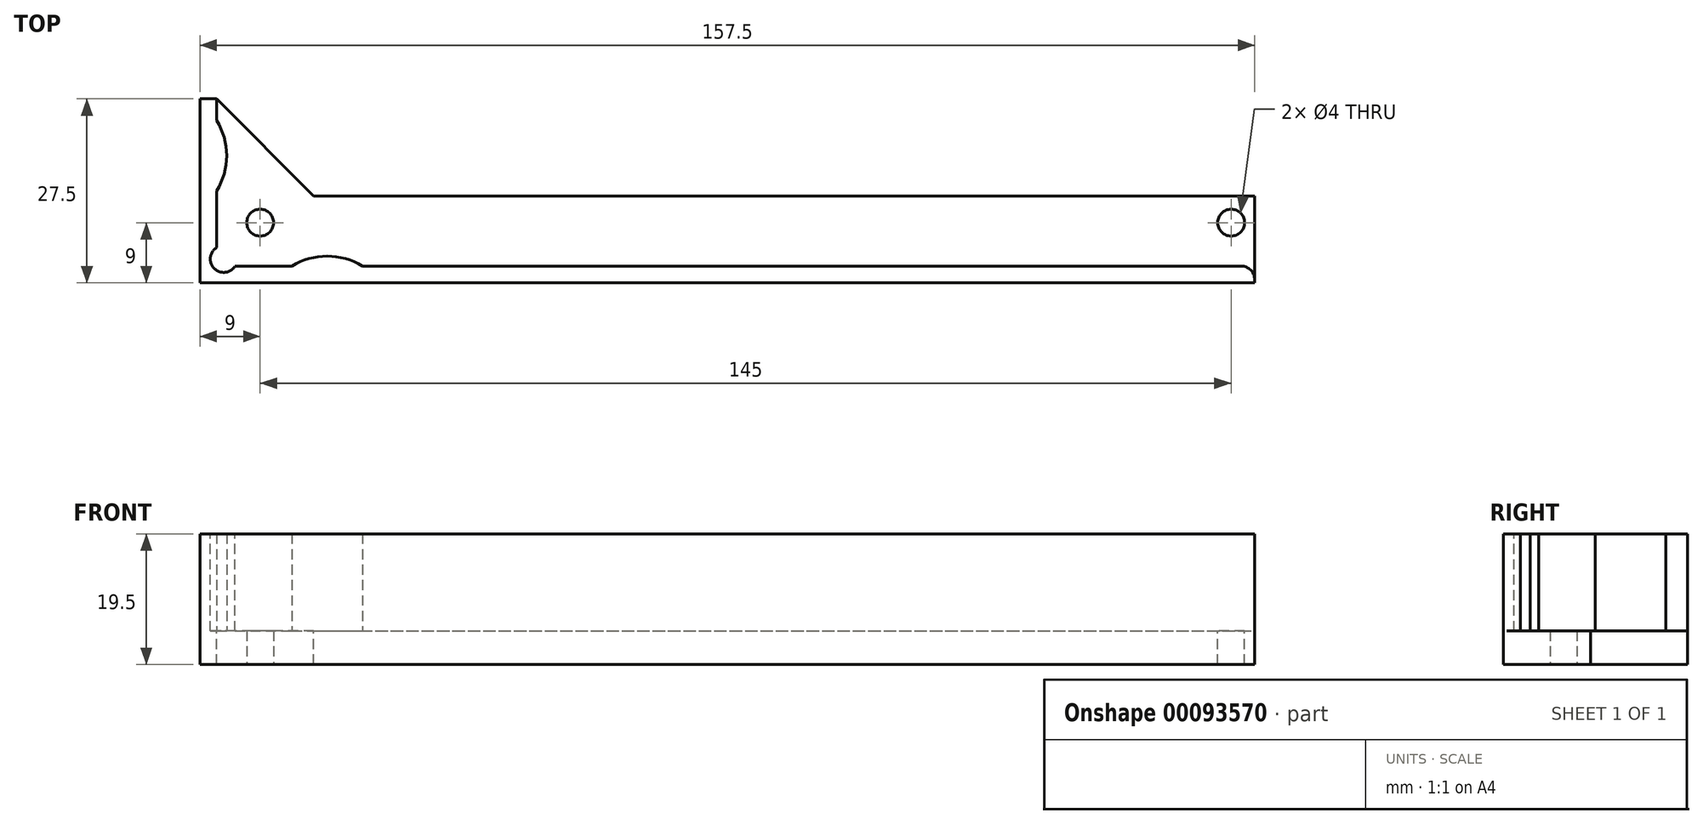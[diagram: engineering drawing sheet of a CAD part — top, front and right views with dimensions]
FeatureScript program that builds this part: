
annotation { "Feature Type Name" : "Feature", "Feature Type Description" : "" }
export const myFeature = defineFeature(function(context is Context, id is Id, definition is map)
    precondition{}
    {
        {
            var Q0;
            Q0=qCreatedBy(makeId("Top.planeOp"),FACE);
            var sketch = newSketch(context, id + "F0", { "sketchPlane" : qUnion([Q0])});
            skCircle(sketch, "E0", {"center": v(0, 0) * mm, "radius": 2 * mm});
            skLineSegment(sketch, "E1", {"start": v(-9, -21) * mm, "end": v(-9, 9) * mm});
            skLineSegment(sketch, "E2", {"start": v(-9, 9) * mm, "end": v(21, 9) * mm});
            skLineSegment(sketch, "E3", {"start": v(21, 9) * mm, "end": v(-9, -21) * mm});
            skSolve(sketch);
        }
        {
            var Q0;
            Q0=qSketchRegion(id+"F0",true);
            extrude(context, id + "F1", {"entities" : qUnion([Q0]), "depth" : 5 * mm});
        }
        {
            var Q0;
            Q0=makeQuery(id+"F1.opExtrude","CAP_FACE",FACE,{"disambiguationData":[OSD([sQuery(id+"F0.wireOp",EDGE,"E0"),sQuery(id+"F0.wireOp",EDGE,"E1"),sQuery(id+"F0.wireOp",EDGE,"E2"),sQuery(id+"F0.wireOp",EDGE,"E3")])],"isStart":false});
            var sketch = newSketch(context, id + "F2", { "sketchPlane" : qUnion([Q0])});
            skLineSegment(sketch, "E4.0", {"start": v(-9, -21) * mm, "end": v(-9, 9) * mm});
            skLineSegment(sketch, "E5.0", {"start": v(-9, 9) * mm, "end": v(21, 9) * mm});
            skLineSegment(sketch, "E6", {"start": v(-9, -21) * mm, "end": v(-6.5, -18.5) * mm});
            skLineSegment(sketch, "E7", {"start": v(-6.5, -18.5) * mm, "end": v(-6.5, 6.5) * mm});
            skLineSegment(sketch, "E8", {"start": v(-6.5, 6.5) * mm, "end": v(18.5, 6.5) * mm});
            skLineSegment(sketch, "E9", {"start": v(18.5, 6.5) * mm, "end": v(21, 9) * mm});
            skSolve(sketch);
        }
        {
            var Q0;
            Q0=qSketchRegion(id+"F2",true);
            extrude(context, id + "F3", {"entities" : qUnion([Q0]), "operationType" : NewBodyOperationType.ADD, "depth" : 14.5 * mm});
        }
        {
            var Q0;
            Q0=makeQuery(id+"F3.opExtrude","CAP_FACE",FACE,{"disambiguationData":[OSD([sQuery(id+"F2.wireOp",EDGE,"E4.0"),sQuery(id+"F2.wireOp",EDGE,"E5.0"),sQuery(id+"F2.wireOp",EDGE,"E6"),sQuery(id+"F2.wireOp",EDGE,"E7"),sQuery(id+"F2.wireOp",EDGE,"E8"),sQuery(id+"F2.wireOp",EDGE,"E9")])],"isStart":false});
            var sketch = newSketch(context, id + "F4", { "sketchPlane" : qUnion([Q0])});
            skLineSegment(sketch, "E10", {"start": v(-6.5, 6.5) * mm, "end": v(0, 0) * mm, "construction": true});
            skCircle(sketch, "E11", {"center": v(-5.44, 5.44) * mm, "radius": 2 * mm});
            skSolve(sketch);
        }
        {
            var Q0;
            Q0=qSketchRegion(id+"F4",true);
            var Q1;
            Q1=makeQuery(id+"F1.opExtrude","CAP_FACE",FACE,{"disambiguationData":[OSD([sQuery(id+"F0.wireOp",EDGE,"E0"),sQuery(id+"F0.wireOp",EDGE,"E1"),sQuery(id+"F0.wireOp",EDGE,"E2"),sQuery(id+"F0.wireOp",EDGE,"E3")])],"isStart":false});
            extrude(context, id + "F5", {"entities" : qUnion([Q0]), "operationType" : NewBodyOperationType.REMOVE, "endBound" : BoundingType.UP_TO_SURFACE, "oppositeDirection" : true, "endBoundEntityFace" : qUnion([Q1]), "depth" : 25 * mm});
        }
        {
            var Q0;
            Q0=makeQuery(id+"F3.opExtrude","CAP_FACE",FACE,{"disambiguationData":[OSD([sQuery(id+"F2.wireOp",EDGE,"E4.0"),sQuery(id+"F2.wireOp",EDGE,"E5.0"),sQuery(id+"F2.wireOp",EDGE,"E6"),sQuery(id+"F2.wireOp",EDGE,"E7"),sQuery(id+"F2.wireOp",EDGE,"E8"),sQuery(id+"F2.wireOp",EDGE,"E9")])],"isStart":false});
            var sketch = newSketch(context, id + "F6", { "sketchPlane" : qUnion([Q0])});
            skLineSegment(sketch, "E12", {"start": v(18.5, 6.5) * mm, "end": v(18.5, 18.97) * mm});
            skLineSegment(sketch, "E13", {"start": v(18.5, 18.97) * mm, "end": v(25.37, 18.97) * mm});
            skLineSegment(sketch, "E14", {"start": v(25.37, 18.97) * mm, "end": v(25.37, -18.5) * mm});
            skLineSegment(sketch, "E15", {"start": v(25.37, -18.5) * mm, "end": v(18.5, 6.5) * mm});
            skLineSegment(sketch, "E16", {"start": v(-6.5, -18.5) * mm, "end": v(-15.6, -18.5) * mm});
            skLineSegment(sketch, "E17", {"start": v(-15.6, -18.5) * mm, "end": v(-15.6, -31.56) * mm});
            skLineSegment(sketch, "E18", {"start": v(-15.6, -31.56) * mm, "end": v(-4.83, -31.56) * mm});
            skLineSegment(sketch, "E19", {"start": v(-4.83, -31.56) * mm, "end": v(-6.5, -18.5) * mm});
            skSolve(sketch);
        }
        {
            var Q0;
            Q0=qSketchRegion(id+"F6",true);
            extrude(context, id + "F7", {"entities" : qUnion([Q0]), "operationType" : NewBodyOperationType.REMOVE, "oppositeDirection" : true, "depth" : 25 * mm});
        }
        {
            var Q0;
            Q0=makeQuery(id+"F5.boolean.opBoolean","MERGE",FACE,{"derivedFrom":[makeQuery(id+"F1.opExtrude","CAP_FACE",FACE,{"disambiguationData":[OSD([sQuery(id+"F0.wireOp",EDGE,"E0"),sQuery(id+"F0.wireOp",EDGE,"E1"),sQuery(id+"F0.wireOp",EDGE,"E2"),sQuery(id+"F0.wireOp",EDGE,"E3")])],"isStart":false})],"fromTools":[makeQuery(id+"F5.opExtrude","CAP_FACE",FACE,{"disambiguationData":[OSD([sQuery(id+"F4.wireOp",EDGE,"E11")])],"isStart":false})]});
            var sketch = newSketch(context, id + "F8", { "sketchPlane" : qUnion([Q0])});
            skLineSegment(sketch, "E20", {"start": v(18.5, 6.5) * mm, "end": v(8, -4) * mm});
            skLineSegment(sketch, "E21", {"start": v(8, -4) * mm, "end": v(18.5, -4) * mm});
            skLineSegment(sketch, "E22", {"start": v(18.5, -4) * mm, "end": v(18.5, 6.5) * mm});
            skSolve(sketch);
        }
        {
            var Q0;
            Q0=qSketchRegion(id+"F8",true);
            var Q1;
            Q1=makeQuery(id+"F1.opExtrude","CAP_FACE",FACE,{"disambiguationData":[OSD([sQuery(id+"F0.wireOp",EDGE,"E0"),sQuery(id+"F0.wireOp",EDGE,"E1"),sQuery(id+"F0.wireOp",EDGE,"E2"),sQuery(id+"F0.wireOp",EDGE,"E3")])],"isStart":true});
            extrude(context, id + "F9", {"entities" : qUnion([Q0]), "operationType" : NewBodyOperationType.ADD, "endBound" : BoundingType.UP_TO_SURFACE, "oppositeDirection" : true, "endBoundEntityFace" : qUnion([Q1]), "depth" : 25 * mm});
        }
        {
            var Q0;
            Q0=makeQuery(id+"F9.boolean.opBoolean","MERGE",FACE,{"derivedFrom":[makeQuery(id+"F7.boolean.opBoolean","COPY",FACE,{"derivedFrom":makeQuery(id+"F7.opExtrude","SWEPT_FACE",FACE,{"disambiguationData":[OSD([sQuery(id+"F6.wireOp",EDGE,"E12")])]})}),makeQuery(id+"F9.opExtrude","SWEPT_FACE",FACE,{"disambiguationData":[OSD([sQuery(id+"F8.wireOp",EDGE,"E22")])]})]});
            var sketch = newSketch(context, id + "F10", { "sketchPlane" : qUnion([Q0])});
            skLineSegment(sketch, "E23.0", {"start": v(-4, 0) * mm, "end": v(9, 0) * mm});
            skLineSegment(sketch, "E23.1", {"start": v(9, 19.5) * mm, "end": v(9, 0) * mm});
            skLineSegment(sketch, "E23.2", {"start": v(6.5, 19.5) * mm, "end": v(9, 19.5) * mm});
            skLineSegment(sketch, "E23.3", {"start": v(6.5, 19.5) * mm, "end": v(6.5, 5) * mm});
            skLineSegment(sketch, "E24.0", {"start": v(-4, 5) * mm, "end": v(6.5, 5) * mm});
            skLineSegment(sketch, "E25.0", {"start": v(-4, 0) * mm, "end": v(-4, 5) * mm});
            skSolve(sketch);
        }
        {
            var Q0;
            Q0=qSketchRegion(id+"F10",true);
            extrude(context, id + "F11", {"entities" : qUnion([Q0]), "operationType" : NewBodyOperationType.ADD, "depth" : 154 * mm});
        }
        {
            var Q0;
            Q0=makeQuery(id+"F11.boolean.opBoolean","MERGE",FACE,{"derivedFrom":[makeQuery(id+"F9.boolean.opBoolean","MERGE",FACE,{"derivedFrom":[makeQuery(id+"F5.boolean.opBoolean","MERGE",FACE,{"derivedFrom":[makeQuery(id+"F1.opExtrude","CAP_FACE",FACE,{"disambiguationData":[OSD([sQuery(id+"F0.wireOp",EDGE,"E0"),sQuery(id+"F0.wireOp",EDGE,"E1"),sQuery(id+"F0.wireOp",EDGE,"E2"),sQuery(id+"F0.wireOp",EDGE,"E3")])],"isStart":false})],"fromTools":[makeQuery(id+"F5.opExtrude","CAP_FACE",FACE,{"disambiguationData":[OSD([sQuery(id+"F4.wireOp",EDGE,"E11")])],"isStart":false})]}),makeQuery(id+"F9.opExtrude","CAP_FACE",FACE,{"disambiguationData":[OSD([sQuery(id+"F8.wireOp",EDGE,"E20"),sQuery(id+"F8.wireOp",EDGE,"E21"),sQuery(id+"F8.wireOp",EDGE,"E22")])],"isStart":true})]}),makeQuery(id+"F11.opExtrude","SWEPT_FACE",FACE,{"disambiguationData":[OSD([sQuery(id+"F10.wireOp",EDGE,"E24.0")])]})]});
            var sketch = newSketch(context, id + "F12", { "sketchPlane" : qUnion([Q0])});
            skLineSegment(sketch, "E26", {"start": v(0, 0) * mm, "end": v(186.25, 0) * mm, "construction": true});
            skCircle(sketch, "E27", {"center": v(145, 0) * mm, "radius": 2 * mm});
            skLineSegment(sketch, "E28.bottom", {"start": v(148.5, 21.9) * mm, "end": v(192.55, 21.9) * mm});
            skLineSegment(sketch, "E28.top", {"start": v(148.5, -50.47) * mm, "end": v(192.55, -50.47) * mm});
            skLineSegment(sketch, "E28.left", {"start": v(148.5, 21.9) * mm, "end": v(148.5, -50.47) * mm});
            skLineSegment(sketch, "E28.right", {"start": v(192.55, 21.9) * mm, "end": v(192.55, -50.47) * mm});
            skPoint(sketch, "E28.middle", {"position": v(170.52, -14.29) * mm});
            skSolve(sketch);
        }
        {
            var Q0;
            Q0=qSketchRegion(id+"F12",true);
            extrude(context, id + "F13", {"entities" : qUnion([Q0]), "operationType" : NewBodyOperationType.REMOVE, "oppositeDirection" : true, "depth" : 30 * mm, "symmetric" : true});
        }
        {
            var Q0;
            Q0=makeQuery(id+"F11.boolean.opBoolean","MERGE",FACE,{"derivedFrom":[makeQuery(id+"F9.boolean.opBoolean","MERGE",FACE,{"derivedFrom":[makeQuery(id+"F5.boolean.opBoolean","MERGE",FACE,{"derivedFrom":[makeQuery(id+"F1.opExtrude","CAP_FACE",FACE,{"disambiguationData":[OSD([sQuery(id+"F0.wireOp",EDGE,"E0"),sQuery(id+"F0.wireOp",EDGE,"E1"),sQuery(id+"F0.wireOp",EDGE,"E2"),sQuery(id+"F0.wireOp",EDGE,"E3")])],"isStart":false})],"fromTools":[makeQuery(id+"F5.opExtrude","CAP_FACE",FACE,{"disambiguationData":[OSD([sQuery(id+"F4.wireOp",EDGE,"E11")])],"isStart":false})]}),makeQuery(id+"F9.opExtrude","CAP_FACE",FACE,{"disambiguationData":[OSD([sQuery(id+"F8.wireOp",EDGE,"E20"),sQuery(id+"F8.wireOp",EDGE,"E21"),sQuery(id+"F8.wireOp",EDGE,"E22")])],"isStart":true})]}),makeQuery(id+"F11.opExtrude","SWEPT_FACE",FACE,{"disambiguationData":[OSD([sQuery(id+"F10.wireOp",EDGE,"E24.0")])]})]});
            var sketch = newSketch(context, id + "F14", { "sketchPlane" : qUnion([Q0])});
            skLineSegment(sketch, "E29", {"start": v(10, 22.12) * mm, "end": v(10, -7.83) * mm, "construction": true});
            skLineSegment(sketch, "E30", {"start": v(-21.03, -10) * mm, "end": v(4.94, -10) * mm, "construction": true});
            skArc(sketch, "E31", {"start": v(4.73, 6.5) * mm, "mid": v(10, 5) * mm, "end": v(15.27, 6.5) * mm});
            skArc(sketch, "E32", {"start": v(-6.5, -15.27) * mm, "mid": v(-5, -10) * mm, "end": v(-6.5, -4.73) * mm});
            skLineSegment(sketch, "E33", {"start": v(-6.5, -15.27) * mm, "end": v(-6.5, -4.73) * mm});
            skLineSegment(sketch, "E34", {"start": v(4.73, 6.5) * mm, "end": v(15.27, 6.5) * mm});
            skSolve(sketch);
        }
        {
            var Q0;
            Q0=qSketchRegion(id+"F14",true);
            var Q1;
            Q1=makeQuery(id+"F11.boolean.opBoolean","MERGE",FACE,{"derivedFrom":[makeQuery(id+"F3.opExtrude","CAP_FACE",FACE,{"disambiguationData":[OSD([sQuery(id+"F2.wireOp",EDGE,"E4.0"),sQuery(id+"F2.wireOp",EDGE,"E5.0"),sQuery(id+"F2.wireOp",EDGE,"E6"),sQuery(id+"F2.wireOp",EDGE,"E7"),sQuery(id+"F2.wireOp",EDGE,"E8"),sQuery(id+"F2.wireOp",EDGE,"E9")])],"isStart":false}),makeQuery(id+"F11.opExtrude","SWEPT_FACE",FACE,{"disambiguationData":[OSD([sQuery(id+"F10.wireOp",EDGE,"E23.2")])]})]});
            extrude(context, id + "F15", {"entities" : qUnion([Q0]), "operationType" : NewBodyOperationType.ADD, "endBound" : BoundingType.UP_TO_SURFACE, "endBoundEntityFace" : qUnion([Q1]), "depth" : 25 * mm});
        }
        {
            var Q0;
            Q0=makeQuery(id+"F13.boolean.opBoolean","INTERSECT",EDGE,{"derivedFrom":[makeQuery(id+"F11.boolean.opBoolean","MERGE",FACE,{"derivedFrom":[makeQuery(id+"F3.opExtrude","SWEPT_FACE",FACE,{"disambiguationData":[OSD([sQuery(id+"F2.wireOp",EDGE,"E8")])]}),makeQuery(id+"F11.opExtrude","SWEPT_FACE",FACE,{"disambiguationData":[OSD([sQuery(id+"F10.wireOp",EDGE,"E23.3")])]})]}),makeQuery(id+"F13.opExtrude","SWEPT_FACE",FACE,{"disambiguationData":[OSD([sQuery(id+"F12.wireOp",EDGE,"E28.left")])]})]});
            fillet(context, id + "F16", {"entities" : qUnion([Q0]), "radius" : 2 * mm, "tangentPropagation" : true, "allowEdgeOverflow" : false});
        }
        {
            var Q0;
            Q0=makeQuery(id+"F1.opExtrude","SWEPT_BODY",BODY,{"disambiguationData":[OSD([sQuery(id+"F0.wireOp",EDGE,"E0"),sQuery(id+"F0.wireOp",EDGE,"E1"),sQuery(id+"F0.wireOp",EDGE,"E2"),sQuery(id+"F0.wireOp",EDGE,"E3")])]});
            var Q1;
            Q1=makeQuery(id+"F11.boolean.opBoolean","MERGE",FACE,{"derivedFrom":[makeQuery(id+"F3.boolean.opBoolean","MERGE",FACE,{"derivedFrom":[makeQuery(id+"F1.opExtrude","SWEPT_FACE",FACE,{"disambiguationData":[OSD([sQuery(id+"F0.wireOp",EDGE,"E2")])]}),makeQuery(id+"F3.opExtrude","SWEPT_FACE",FACE,{"disambiguationData":[OSD([sQuery(id+"F2.wireOp",EDGE,"E5.0")])]})]}),makeQuery(id+"F11.opExtrude","SWEPT_FACE",FACE,{"disambiguationData":[OSD([sQuery(id+"F10.wireOp",EDGE,"E23.1")])]})]});
            mirror(context, id + "F17", {"entities" : qUnion([Q0]), "mirrorPlane" : qUnion([Q1])});
        }
        {
            var Q0;
            Q0=makeQuery(id+"F1.opExtrude","SWEPT_BODY",BODY,{"disambiguationData":[OSD([sQuery(id+"F0.wireOp",EDGE,"E0"),sQuery(id+"F0.wireOp",EDGE,"E1"),sQuery(id+"F0.wireOp",EDGE,"E2"),sQuery(id+"F0.wireOp",EDGE,"E3")])]});
            deleteBodies(context, id + "F18", {"entities" : qUnion([Q0])});
        }
    });
